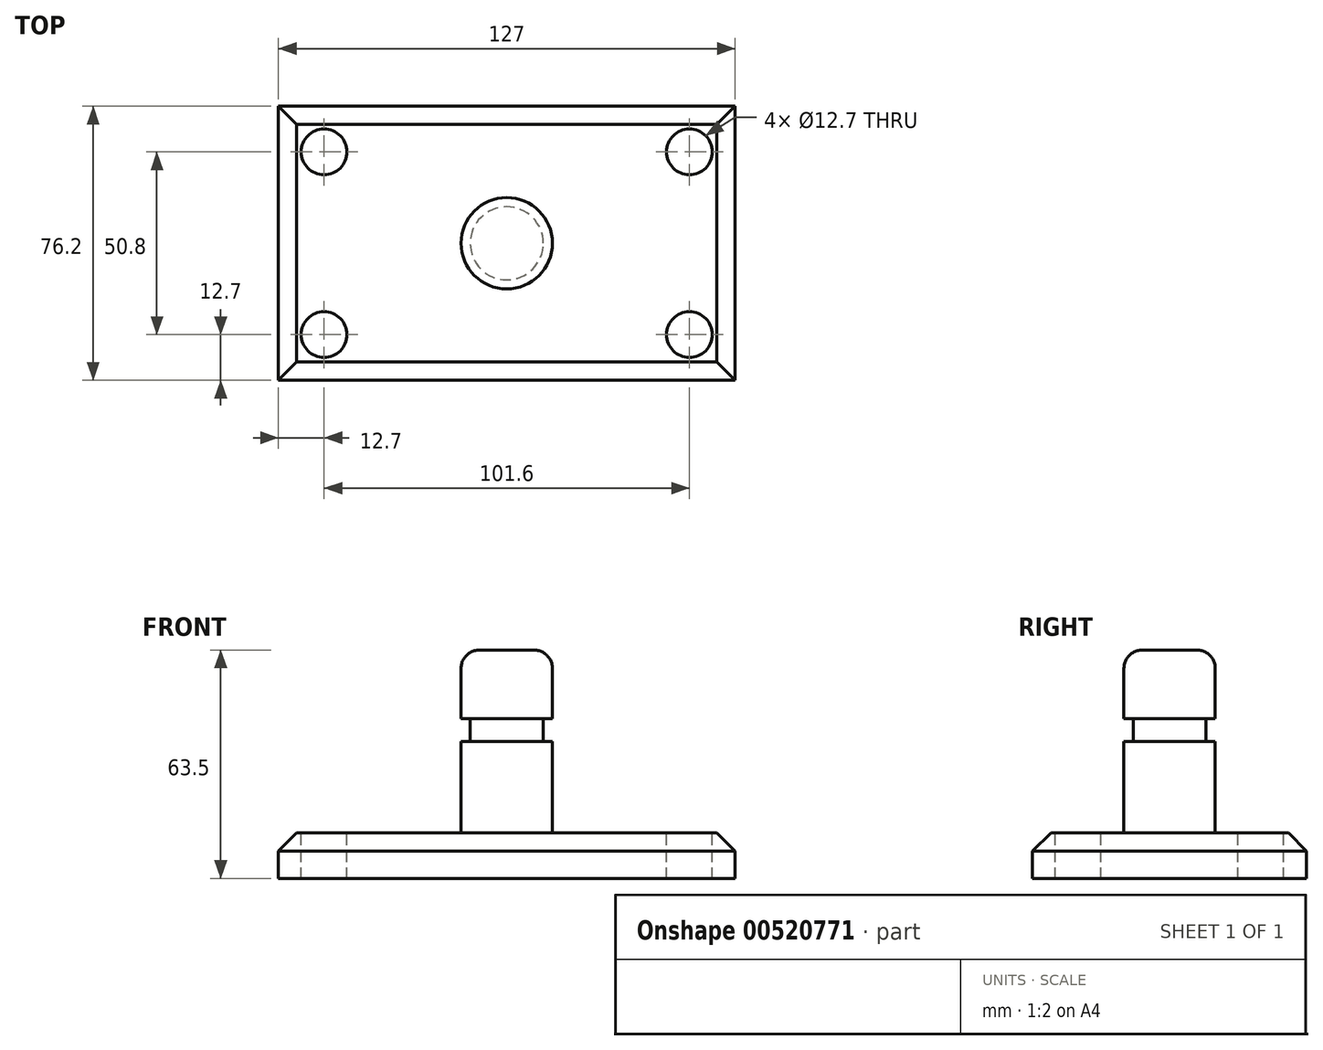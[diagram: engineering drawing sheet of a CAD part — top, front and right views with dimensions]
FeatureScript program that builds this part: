
annotation { "Feature Type Name" : "Feature", "Feature Type Description" : "" }
export const myFeature = defineFeature(function(context is Context, id is Id, definition is map)
    precondition{}
    {
        {
            var Q0;
            Q0=qCreatedBy(makeId("Top.planeOp"),FACE);
            var sketch = newSketch(context, id + "F0", { "sketchPlane" : qUnion([Q0])});
            skLineSegment(sketch, "E0.bottom", {"start": v(63.5, 38.1) * mm, "end": v(-63.5, 38.1) * mm});
            skLineSegment(sketch, "E0.top", {"start": v(63.5, -38.1) * mm, "end": v(-63.5, -38.1) * mm});
            skLineSegment(sketch, "E0.left", {"start": v(63.5, 38.1) * mm, "end": v(63.5, -38.1) * mm});
            skLineSegment(sketch, "E0.right", {"start": v(-63.5, 38.1) * mm, "end": v(-63.5, -38.1) * mm});
            skPoint(sketch, "E0.middle", {"position": v(0, 0) * mm});
            skSolve(sketch);
        }
        {
            var Q0;
            Q0=makeQuery(id+"F0.imprint","IMPRINT",FACE,{"disambiguationData":[TD([[makeQuery(id+"F0.imprint","IMPRINT",EDGE,{"derivedFrom":sQuery(id+"F0.wireOp",EDGE,"E0.bottom")}),1.0]])]});
            extrude(context, id + "F1", {"entities" : qUnion([Q0]), "depth" : 12.7 * mm, "offsetDistance" : 25.4 * mm});
        }
        {
            var Q0;
            Q0=makeQuery(id+"F1.opExtrude","CAP_FACE",FACE,{"disambiguationData":[OSD([sQuery(id+"F0.wireOp",EDGE,"E0.bottom"),sQuery(id+"F0.wireOp",EDGE,"E0.top"),sQuery(id+"F0.wireOp",EDGE,"E0.left"),sQuery(id+"F0.wireOp",EDGE,"E0.right")])],"isStart":false});
            var sketch = newSketch(context, id + "F2", { "sketchPlane" : qUnion([Q0])});
            skCircle(sketch, "E1", {"center": v(-50.8, -25.4) * mm, "radius": 6.35 * mm});
            skCircle(sketch, "E2", {"center": v(-50.8, 25.4) * mm, "radius": 6.35 * mm});
            skCircle(sketch, "E3", {"center": v(50.8, -25.4) * mm, "radius": 6.35 * mm});
            skCircle(sketch, "E4", {"center": v(50.8, 25.4) * mm, "radius": 6.35 * mm});
            skSolve(sketch);
        }
        {
            var Q0;
            Q0 = qSketchRegion(id + "F2", true);
            extrude(context, id + "F3", {"entities" : qUnion([Q0]), "operationType" : NewBodyOperationType.REMOVE, "endBound" : BoundingType.THROUGH_ALL, "oppositeDirection" : true, "depth" : 25.4 * mm, "offsetDistance" : 25.4 * mm});
        }
        {
            var Q0;
            Q0=qCreatedBy(makeId("Front.planeOp"),FACE);
            var sketch = newSketch(context, id + "F4", { "sketchPlane" : qUnion([Q0])});
            skLineSegment(sketch, "E5.bottom", {"start": v(0, 12.7) * mm, "end": v(12.7, 12.7) * mm});
            skLineSegment(sketch, "E5.top", {"start": v(0, 63.5) * mm, "end": v(12.7, 63.5) * mm});
            skLineSegment(sketch, "E5.left", {"start": v(0, 12.7) * mm, "end": v(0, 63.5) * mm});
            skLineSegment(sketch, "E5.right", {"start": v(12.7, 12.7) * mm, "end": v(12.7, 63.5) * mm});
            skSolve(sketch);
        }
        {
            var Q0;
            Q0=makeQuery(id+"F4.imprint","IMPRINT",FACE,{"disambiguationData":[TD([[makeQuery(id+"F4.imprint","IMPRINT",EDGE,{"derivedFrom":sQuery(id+"F4.wireOp",EDGE,"E5.bottom")}),1.0]])]});
            var Q1;
            Q1=sQuery(id+"F4.wireOp",EDGE,"E5.left");
            revolve(context, id + "F5", {"operationType" : NewBodyOperationType.ADD, "entities" : qUnion([Q0]), "axis" : qUnion([Q1]), "revolveType" : RevolveType.FULL});
        }
        {
            var Q0;
            Q0=qCreatedBy(makeId("Front.planeOp"),FACE);
            var sketch = newSketch(context, id + "F6", { "sketchPlane" : qUnion([Q0])});
            skLineSegment(sketch, "E6.bottom", {"start": v(19.42, 44.45) * mm, "end": v(10.16, 44.45) * mm});
            skLineSegment(sketch, "E6.top", {"start": v(19.42, 38.1) * mm, "end": v(10.16, 38.1) * mm});
            skLineSegment(sketch, "E6.left", {"start": v(19.42, 44.45) * mm, "end": v(19.42, 38.1) * mm});
            skLineSegment(sketch, "E6.right", {"start": v(10.16, 44.45) * mm, "end": v(10.16, 38.1) * mm});
            skSolve(sketch);
        }
        {
            var Q0;
            Q0=makeQuery(id+"F6.imprint","IMPRINT",FACE,{"disambiguationData":[TD([[makeQuery(id+"F6.imprint","IMPRINT",EDGE,{"derivedFrom":sQuery(id+"F6.wireOp",EDGE,"E6.bottom")}),1.0]])]});
            var Q1;
            Q1=makeQuery(id+"F5.opRevolve","SWEPT_FACE",FACE,{"disambiguationData":[OSD([sQuery(id+"F4.wireOp",EDGE,"E5.right")])]});
            revolve(context, id + "F7", {"operationType" : NewBodyOperationType.REMOVE, "entities" : qUnion([Q0]), "axis" : qUnion([Q1]), "revolveType" : RevolveType.FULL, "oppositeDirection" : true});
        }
        {
            var Q0;
            Q0=makeQuery(id+"F5.opRevolve","SWEPT_FACE",FACE,{"disambiguationData":[OSD([sQuery(id+"F4.wireOp",EDGE,"E5.top")])]});
            var Q1;
            Q1=makeQuery(id+"F5.opRevolve","SWEPT_EDGE",EDGE,{"disambiguationData":[OSD([sQuery(id+"F4.wireOp",EDGE,"E5.bottom"),sQuery(id+"F4.wireOp",EDGE,"E5.right")])]});
            fillet(context, id + "F8", {"entities" : qUnion([Q0, Q1]), "radius" : 5.08 * mm, "tangentPropagation" : true, "allowEdgeOverflow" : false});
        }
        {
            var Q0;
            Q0=makeQuery(id+"F1.opExtrude","CAP_EDGE",EDGE,{"disambiguationData":[OSD([sQuery(id+"F0.wireOp",EDGE,"E0.right")])],"isStart":false});
            var Q1;
            Q1=makeQuery(id+"F1.opExtrude","CAP_EDGE",EDGE,{"disambiguationData":[OSD([sQuery(id+"F0.wireOp",EDGE,"E0.top")])],"isStart":false});
            var Q2;
            Q2=makeQuery(id+"F1.opExtrude","CAP_EDGE",EDGE,{"disambiguationData":[OSD([sQuery(id+"F0.wireOp",EDGE,"E0.bottom")])],"isStart":false});
            var Q3;
            Q3=makeQuery(id+"F1.opExtrude","CAP_EDGE",EDGE,{"disambiguationData":[OSD([sQuery(id+"F0.wireOp",EDGE,"E0.left")])],"isStart":false});
            chamfer(context, id + "F9", {"entities" : qUnion([Q0, Q1, Q2, Q3]), "width" : 5.08 * mm, "tangentPropagation" : true});
        }
    });
